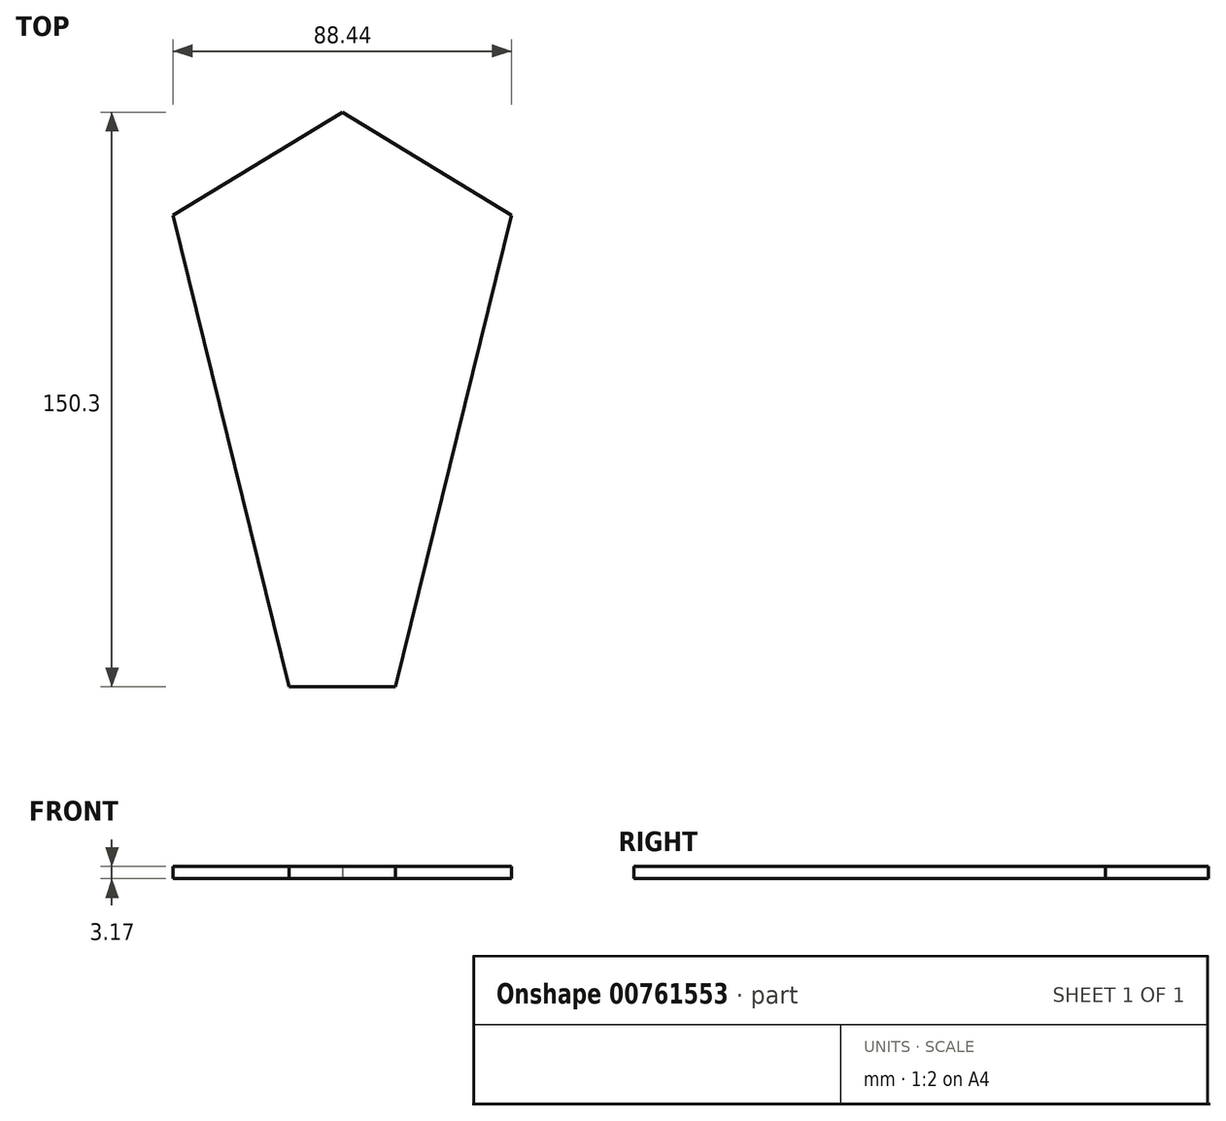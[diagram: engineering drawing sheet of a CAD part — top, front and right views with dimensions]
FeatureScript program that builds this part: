
annotation { "Feature Type Name" : "Feature", "Feature Type Description" : "" }
export const myFeature = defineFeature(function(context is Context, id is Id, definition is map)
    precondition{}
    {
        {
            var Q0;
            Q0=qCreatedBy(makeId("Top.planeOp"),FACE);
            var sketch = newSketch(context, id + "F0", { "sketchPlane" : qUnion([Q0])});
            skLineSegment(sketch, "E0.5", {"start": v(-149.68, 94.83) * mm, "end": v(-105.46, 121.8) * mm});
            skLineSegment(sketch, "E1", {"start": v(-149.68, 94.83) * mm, "end": v(-119.41, -28.5) * mm});
            skLineSegment(sketch, "E2", {"start": v(-105.46, -28.5) * mm, "end": v(-119.41, -28.5) * mm});
            skLineSegment(sketch, "E3", {"start": v(-105.46, -28.5) * mm, "end": v(-91.51, -28.5) * mm});
            skLineSegment(sketch, "E4", {"start": v(-105.46, 121.8) * mm, "end": v(-61.24, 94.83) * mm});
            skLineSegment(sketch, "E5", {"start": v(-61.24, 94.83) * mm, "end": v(-91.51, -28.5) * mm});
            skSolve(sketch);
        }
        {
            var Q0;
            Q0 = qSketchRegion(id + "F0", true);
            extrude(context, id + "F1", {"entities" : qUnion([Q0]), "depth" : 3.17 * mm, "offsetDistance" : 25.4 * mm});
        }
    });
